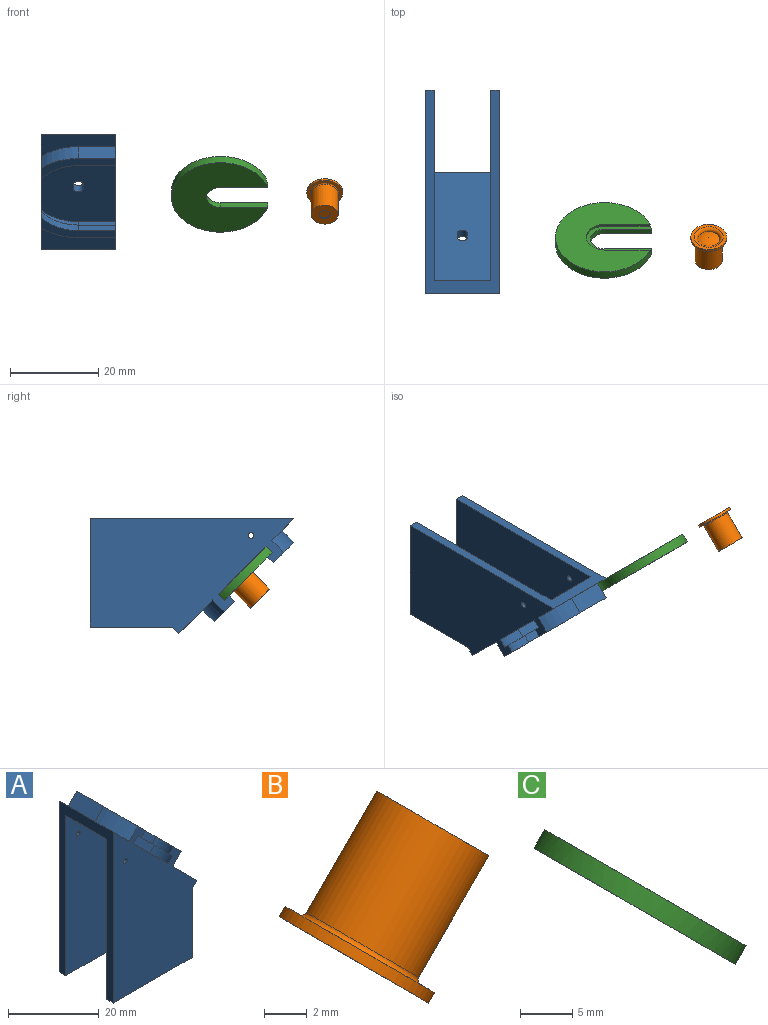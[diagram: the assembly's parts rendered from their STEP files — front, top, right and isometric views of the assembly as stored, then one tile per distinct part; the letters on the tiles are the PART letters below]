
ASSEMBLY  parts=3 mates=2
PART A: 36 faces, bbox 26x16.8x46 mm
  f0: plane 16.76x7.55mm, normal (0.71,0,0.71), area 134.5mm2, adj f2,f4,f16,f18,f35
  f1: plane 16.76x16.07mm, normal (0.71,0,0.71), area 355.3mm2, adj f2,f5,f6,f18,f22,f23,f24,f25
  f2: plane 46x25.97mm, normal (0,1,0), area 842.1mm2, adj f0,f1,f7,f8,f11,f12,f14,f15
  f3: cylinder r=12.7mm len=8.38mm, axis (-0.71,0,-0.71), area 34.9mm2, adj f11,f14,f18,f32
  f4: cylinder r=12.7mm len=8.38mm, axis (-0.71,0,-0.71), area 34.9mm2, adj f0,f12,f18,f35
  f5: cylinder r=11.37mm len=8.38mm, axis (-0.71,0,-0.71), area 19.2mm2, adj f1,f7,f18,f31
  f6: cylinder r=11.37mm len=8.38mm, axis (-0.71,0,-0.71), area 19.2mm2, adj f1,f8,f18,f33
  f7: plane 16.76x3.67mm, normal (-0.71,0,-0.71), area 17.1mm2, adj f2,f5,f9,f18,f30,f31
  f8: plane 16.76x3.67mm, normal (-0.71,0,-0.71), area 17.1mm2, adj f2,f6,f10,f18,f33,f34
  f9: cylinder r=10.41mm len=8.38mm, axis (-0.71,0,-0.71), area 17.3mm2, adj f7,f11,f18,f30
  f10: cylinder r=10.41mm len=8.38mm, axis (-0.71,0,-0.71), area 17.3mm2, adj f8,f12,f18,f34
  f11: plane 16.76x4.61mm, normal (0.71,0,0.71), area 40.7mm2, adj f2,f3,f9,f18,f30,f32
  f12: plane 16.76x4.61mm, normal (0.71,0,0.71), area 40.7mm2, adj f2,f4,f10,f18,f34,f35
  f13: plane 24.54x24.54mm, normal (-0.71,0,-0.71), area 434mm2, adj f15,f16,f17,f19,f22,f23,f24,f25
  f14: plane 16.76x4.93mm, normal (0.71,0,0.71), area 72.2mm2, adj f2,f3,f15,f18,f32
  f15: plane 46x16.76mm, normal (-1,0,0), area 223.5mm2, adj f2,f13,f14,f17,f18,f19,f27,f29
  f16: plane 16.76x1.44mm, normal (0.71,0,-0.71), area 34.1mm2, adj f0,f2,f13,f18,f26,f28
  f17: plane 43.13x24.54mm, normal (0,1,0), area 756mm2, adj f13,f15,f21,f26,f27
  f18: plane 46x25.97mm, normal (0,-1,0), area 848.1mm2, adj f0,f1,f3,f4,f5,f6,f7,f8
  f19: plane 43.13x24.54mm, normal (0,-1,0), area 756mm2, adj f13,f15,f20,f28,f29
  f20: cylinder r=0.64mm len=2.03mm, axis (0,-1,0), area 8.1mm2, adj f2,f19
  f21: cylinder r=0.64mm len=2.03mm, axis (0,-1,0), area 8.1mm2, adj f17,f18
  f22: plane 2.25x2.25mm, normal (0,-1,0), area 2.3mm2, adj f1,f13,f23,f25
  f23: cylinder r=1.14mm len=2.29mm, axis (0.71,0,0.71), area 7.3mm2, adj f1,f13,f22,f24
  f24: plane 2.25x2.25mm, normal (0,1,0), area 2.3mm2, adj f1,f13,f23,f25
  f25: cylinder r=1.14mm len=2.29mm, axis (0.71,0,0.71), area 7.3mm2, adj f1,f13,f22,f24
  f26: plane 18.59x2.03mm, normal (1,0,0), area 37.8mm2, adj f16,f17,f18,f27
  f27: plane 24.54x2.03mm, normal (0,0,-1), area 49.9mm2, adj f15,f17,f18,f26
  f28: plane 18.59x2.03mm, normal (1,0,0), area 37.8mm2, adj f2,f16,f19,f29
  f29: plane 24.54x2.03mm, normal (0,0,-1), area 49.9mm2, adj f2,f15,f19,f28
  f30: plane 8.38x1.26mm, normal (0.71,0,-0.71), area 14.9mm2, adj f2,f7,f9,f11
  f31: plane 8.38x1.44mm, normal (0.71,0,-0.71), area 17mm2, adj f1,f2,f5,f7
  f32: plane 8.38x2.69mm, normal (-0.71,0,0.71), area 31.9mm2, adj f2,f3,f11,f14
  f33: plane 8.38x1.44mm, normal (-0.71,0,0.71), area 17mm2, adj f1,f2,f6,f8
  f34: plane 8.38x1.26mm, normal (-0.71,0,0.71), area 14.9mm2, adj f2,f8,f10,f12
  f35: plane 8.38x2.69mm, normal (0.71,0,-0.71), area 31.9mm2, adj f0,f2,f4,f12
PART B: 10 faces, bbox 10.3x8.4x10.3 mm
  f0: plane 6.1x4.31mm, normal (0.71,0,0.71), area 24.1mm2, adj f1,f9
  f1: cylinder r=3.05mm len=8.98mm, axis (0.71,0,0.71), area 126.5mm2, adj f0,f2
  f2: torus R=3.3mm, axis (0.71,0,0.71), area 7.9mm2, adj f1,f3
  f3: plane 8.13x5.75mm, normal (0.71,0,0.71), area 17.6mm2, adj f2,f4
  f4: cylinder r=4.06mm len=8.13mm, axis (0.71,0,0.71), area 14.3mm2, adj f3,f5
  f5: plane 8.13x5.75mm, normal (-0.71,0,-0.71), area 17.6mm2, adj f4,f6
  f6: torus R=3.3mm, axis (0.71,0,0.71), area 20.8mm2, adj f5,f7
  f7: sphere r=5.88mm, area 20.5mm2, adj f6
  f8: plane 2.54x1.8mm, normal (0.71,0,0.71), area 5.1mm2, adj f9
  f9: cylinder r=1.27mm len=2.54mm, axis (0.71,0,0.71), area 3.1mm2, adj f0,f8
PART C: 10 faces, bbox 17.2x21.8x17.2 mm
  f0: cylinder r=11.11mm len=21.76mm, axis (-0.71,0,-0.71), area 127.6mm2, adj f1,f3,f5,f6,f7,f8,f9
  f1: plane 21.76x15.72mm, normal (0.71,0,0.71), area 302.5mm2, adj f0,f2,f7,f8
  f2: cylinder r=3.17mm len=5.51mm, axis (-0.71,0,-0.71), area 14.4mm2, adj f1,f5,f7,f8
  f3: plane 21.44x15.72mm, normal (-0.71,0,-0.71), area 272.1mm2, adj f0,f4,f6,f9
  f4: cylinder r=4.11mm len=6.23mm, axis (-0.71,0,-0.71), area 7.6mm2, adj f3,f5,f6,f9
  f5: plane 14.76x5.82mm, normal (-0.71,0,-0.71), area 30.5mm2, adj f0,f2,f4,f6,f7,f8,f9
  f6: plane 10.32x0.41mm, normal (-0.71,0,0.71), area 6mm2, adj f0,f3,f4,f5
  f7: plane 10.65x1.02mm, normal (-0.71,0,0.71), area 15.4mm2, adj f0,f1,f2,f5
  f8: plane 10.65x1.02mm, normal (0.71,0,-0.71), area 15.4mm2, adj f0,f1,f2,f5
  f9: plane 10.32x0.41mm, normal (0.71,0,-0.71), area 6mm2, adj f0,f3,f4,f5
PLACE A rot(axis=(0.58,0.58,-0.58),120deg) t=(-8.38,-20.47,-8.89)mm
PLACE B rot(axis=(0.91,-0.16,-0.38),138.6deg) t=(50.26,-21.75,-8.44)mm
PLACE C rot(axis=(0.58,0.58,-0.58),120deg) t=(23.81,-19.36,-10)mm
MATE planar C.f3 <-> A.f1  axis (0,0.71,0.71) through (22.2,-35.1,-21.67)mm
MATE planar B.f2 <-> C.f5  axis (0,-0.71,-0.71) through (47.39,-35.45,-22.15)mm
